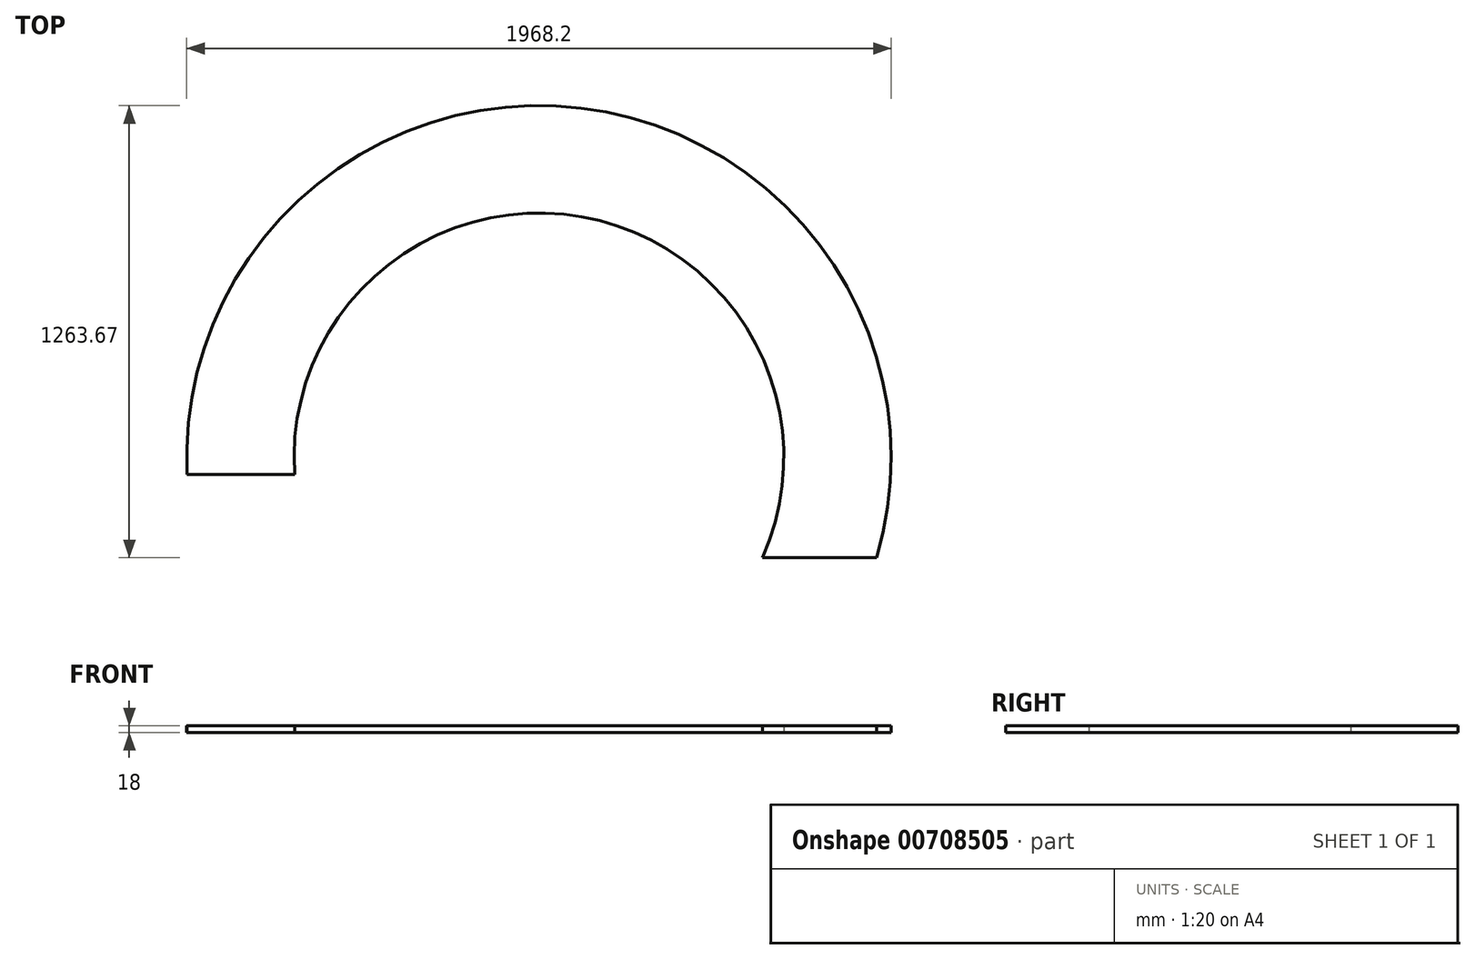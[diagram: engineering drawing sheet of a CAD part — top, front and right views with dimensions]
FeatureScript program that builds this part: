
annotation { "Feature Type Name" : "Feature", "Feature Type Description" : "" }
export const myFeature = defineFeature(function(context is Context, id is Id, definition is map)
    precondition{}
    {
        {
            var Q0;
            Q0=qCreatedBy(makeId("Top.planeOp"),FACE);
            var sketch = newSketch(context, id + "F0", { "sketchPlane" : qUnion([Q0])});
            skPoint(sketch, "E0.middle", {"position": v(0, 0) * mm});
            skPoint(sketch, "E1.end.orphan", {"position": v(-300, -300) * mm});
            skPoint(sketch, "E2.visualSharp", {"position": v(-300, 300) * mm});
            skPoint(sketch, "E3.visualSharp", {"position": v(-300, -52.1) * mm});
            skPoint(sketch, "E4.visualSharp", {"position": v(300, 300) * mm});
            skLineSegment(sketch, "E5", {"start": v(-300, -2.1) * mm, "end": v(-300, -2.1) * mm});
            skPoint(sketch, "E6.visualSharp", {"position": v(-300, -70.1) * mm});
            skArc(sketch, "E7.0", {"start": v(943.55, -279.57) * mm, "mid": v(117.76, 977.03) * mm, "end": v(-982.96, -47.36) * mm});
            skArc(sketch, "E8.0", {"start": v(624.37, -279.57) * mm, "mid": v(119.68, 673.55) * mm, "end": v(-682.46, -47.36) * mm});
            skPoint(sketch, "E9.start.orphan", {"position": v(300, -300) * mm});
            skLineSegment(sketch, "E10", {"start": v(624.37, -279.57) * mm, "end": v(943.55, -279.57) * mm});
            skLineSegment(sketch, "E11", {"start": v(-682.46, -47.36) * mm, "end": v(-982.96, -47.36) * mm});
            skPoint(sketch, "E12.start.orphan", {"position": v(-981.74, -68.13) * mm});
            skPoint(sketch, "E13.end.orphan", {"position": v(-981.74, -70.1) * mm});
            skSolve(sketch);
        }
        {
            var Q0;
            Q0=qSketchRegion(id+"F0",true);
            extrude(context, id + "F1", {"entities" : qUnion([Q0]), "depth" : 18 * mm, "offsetDistance" : 25 * mm});
        }
    });
